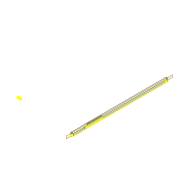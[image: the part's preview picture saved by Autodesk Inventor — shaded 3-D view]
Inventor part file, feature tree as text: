
AUTODESK INVENTOR PART (.ipt)
format: ipt  version: 2022 (Build 260153000, 153)  size: 115,200 bytes
history: native  units: mm
features: sketch x2, extrude x1, projected_geometry x1
ambient origin geometry x8: Origin, YZ Plane, XZ Plane, XY Plane, X Axis, Y Axis, Z Axis, Center Point
bodies: Solid1 (feature_tree)
feature tree (4):
  extrude  "Extrusion1"  Depth=8.0mm
  sketch  "Sketch2"  dims[d2=3.0mm d3=3.0mm d4=8.0mm d5=0.0mm d12=3.0mm d13=50.8mm d14=100.0mm d15=40.0mm d16=200.0mm d17=200.0mm]
  sketch  "Sketch1"  dims[d0=319.927mm d1=8.0mm]
  projected_geometry  "Projected Loop1"
